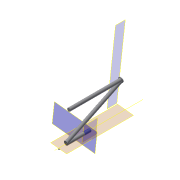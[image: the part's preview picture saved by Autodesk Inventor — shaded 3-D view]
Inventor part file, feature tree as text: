
AUTODESK INVENTOR PART (.ipt)
format: ipt  version: 2022 (Build 260153000, 153)  size: 187,904 bytes
history: native  units: mm
features: other x13, plane x8, sketch x6, projected_geometry x6, reference x4, extrude x3, sweep x1
ambient origin geometry x8: Origin, YZ Plane, XZ Plane, XY Plane, X Axis, Y Axis, Z Axis, Center Point
bodies: Solid1 (feature_tree)
feature tree (41):
  plane  "Work Plane1"
  plane  "Work Plane4"
  sketch  "Sketch1"  dims[d0=40.0mm d1=100.0mm]
  plane  "Work Plane7"
  sweep  "Sweep1"
  plane  "Work Plane8"
  extrude  "Extrusion1"  Depth=85.0mm
  extrude  "Extrusion2"  Depth=12.217305mm
  extrude  "Extrusion3"  TaperAngle=0.0deg  [1 undecoded]
  plane  "Arbeitsebene10"
  sketch  "Skizze7"  dims[d11=7.0mm d12=7.0mm d13=10.0mm d14=0.0mm d15=1.0mm d16=0.0mm d17=1.0mm d18=0.0mm d19=1.4mm d20=1.4mm]
  other  "Work Axis1"
  plane  "Work Plane2"
  other  "Work Point1"
  plane  "Work Plane3"
  sketch  "Sketch3"  dims[d2=30.0deg d3=85.0mm]
  reference  "Reference2"
  sketch  "Sketch4"  dims[d4=30.0deg d6=12.217305mm]
  projected_geometry  "Projected Loop1"
  projected_geometry  "Projected Loop2"
  projected_geometry  "Projected Loop3"
  reference  "Reference3"
  sketch  "Sketch5"  dims[d7=5.0mm d8=0.0mm d9=0.0mm]
  sketch  "Sketch6"  dims[d10=12.217305mm]
  projected_geometry  "Projected Loop4"
  other  "Arbeitsachse2"
  other  "Arbeitspunkt2"
  plane  "Arbeitsebene9"
  projected_geometry  "Projizierte Kontur5"
  reference  "Referenz4"
  reference  "Referenz5"
  projected_geometry  "Projizierte Kontur6"
  other  "cellSTORM_v5.iam"
  other  "10_Filteslide_25mm:1"
  other  "cellSTORM_Base_v0_R1:1"
  other  "<userpath>\Documents\GitHub\cellstorm\INVENTOR\cellSTORM_v6.iam"
  other  "cellSTORM_v6.iam"
  other  "cellSTORM_v5_laserstage:1"
  other  "<userpath>\Downloads\cellSTORM\cellSTORM_v5_microsocpe.iam"
  other  "cellSTORM_v5_microsocpe.iam"
  other  "cellSTORM_v5_opticalstage:1"
note: 1 required parameter value undecoded (feature->parameter linkage not recoverable at this tier; creation-order binding heuristic only, values carry confidence <= 0.55)
